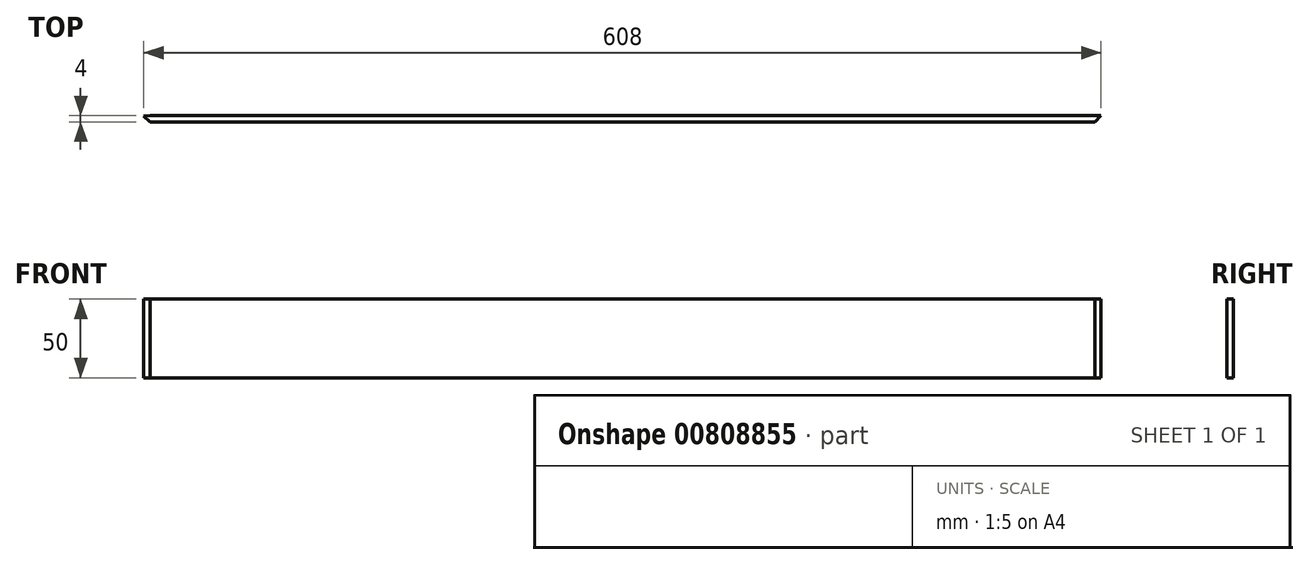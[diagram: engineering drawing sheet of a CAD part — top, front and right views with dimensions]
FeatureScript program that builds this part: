
annotation { "Feature Type Name" : "Feature", "Feature Type Description" : "" }
export const myFeature = defineFeature(function(context is Context, id is Id, definition is map)
    precondition{}
    {
        {
            var Q0;
            Q0=qCreatedBy(makeId("Top.planeOp"),FACE);
            var sketch = newSketch(context, id + "F0", { "sketchPlane" : qUnion([Q0])});
            skLineSegment(sketch, "E0.bottom", {"start": v(0, 0) * mm, "end": v(600, 0) * mm});
            skLineSegment(sketch, "E0.top", {"start": v(0, 4) * mm, "end": v(600, 4) * mm});
            skLineSegment(sketch, "E0.left", {"start": v(0, 0) * mm, "end": v(0, 4) * mm});
            skLineSegment(sketch, "E0.right", {"start": v(600, 0) * mm, "end": v(600, 4) * mm});
            skLineSegment(sketch, "E1", {"start": v(0, 0) * mm, "end": v(-4, 3.94) * mm});
            skLineSegment(sketch, "E2", {"start": v(-4, 3.94) * mm, "end": v(0, 4) * mm});
            skLineSegment(sketch, "E3", {"start": v(600, 0) * mm, "end": v(604, 4) * mm});
            skLineSegment(sketch, "E4", {"start": v(604, 4) * mm, "end": v(600, 4) * mm});
            skSolve(sketch);
        }
        {
            var Q0;
            Q0=makeQuery(id+"F0.imprint","IMPRINT",FACE,{"disambiguationData":[TD([[makeQuery(id+"F0.imprint","IMPRINT",EDGE,{"derivedFrom":sQuery(id+"F0.wireOp",EDGE,"E0.right")}),-1.0]])]});
            var Q1;
            Q1=makeQuery(id+"F0.imprint","IMPRINT",FACE,{"disambiguationData":[TD([[makeQuery(id+"F0.imprint","IMPRINT",EDGE,{"derivedFrom":sQuery(id+"F0.wireOp",EDGE,"E0.bottom")}),1.0]])]});
            var Q2;
            Q2=makeQuery(id+"F0.imprint","IMPRINT",FACE,{"disambiguationData":[TD([[makeQuery(id+"F0.imprint","IMPRINT",EDGE,{"derivedFrom":sQuery(id+"F0.wireOp",EDGE,"E0.left")}),1.0]])]});
            extrude(context, id + "F1", {"entities" : qUnion([Q0, Q1, Q2]), "depth" : 50 * mm, "offsetDistance" : 25 * mm});
        }
    });
